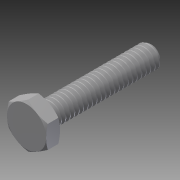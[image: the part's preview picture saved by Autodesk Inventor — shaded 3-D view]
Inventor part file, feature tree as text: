
AUTODESK INVENTOR PART (.ipt)
format: ipt  version: 2014 SP1 (Build 180222100, 222)  size: 836,608 bytes
history: native  units: in
note: dims shown in document units (in); Inventor stores cm internally (conversion verified against a paired STEP export)
features: extrude x1, other x1, imported_body x1
ambient origin geometry x8: Origin, YZ Plane, XZ Plane, XY Plane, X Axis, Y Axis, Z Axis, Center Point
bodies: Body1 (feature_tree)
feature tree (3):
  extrude  "Extrude14"  [1 undecoded]
  other  "92620A5441"
  imported_body  "Base1"
note: 1 required parameter value undecoded (feature->parameter linkage not recoverable at this tier; creation-order binding heuristic only, values carry confidence <= 0.55)
